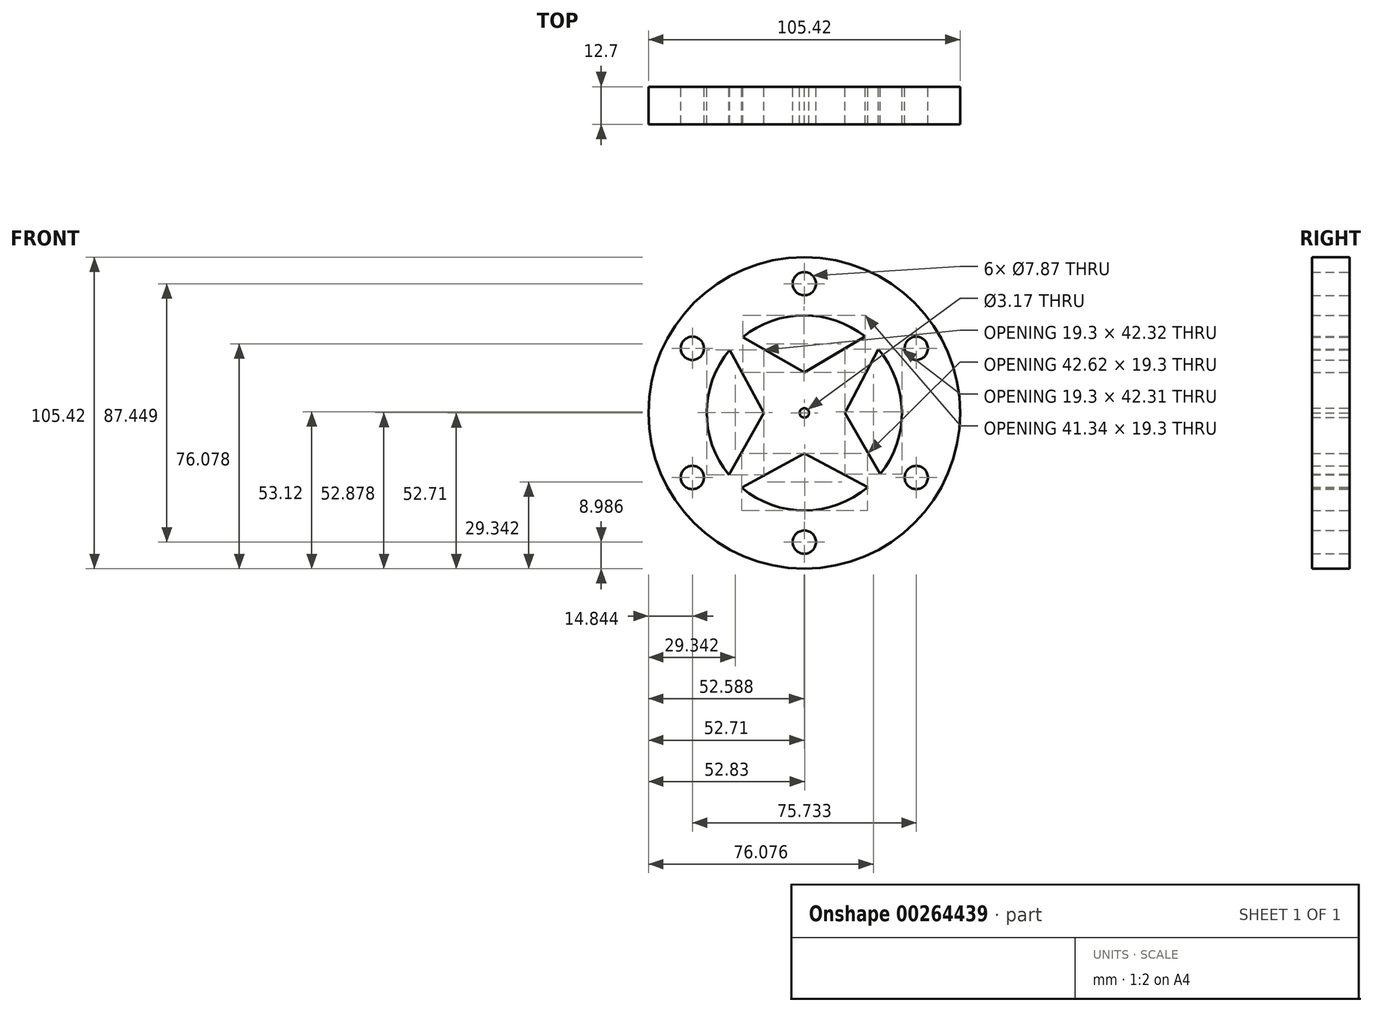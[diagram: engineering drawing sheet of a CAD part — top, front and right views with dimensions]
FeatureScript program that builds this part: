
annotation { "Feature Type Name" : "Feature", "Feature Type Description" : "" }
export const myFeature = defineFeature(function(context is Context, id is Id, definition is map)
    precondition{}
    {
        {
            var Q0;
            Q0=qCreatedBy(makeId("Front.planeOp"),FACE);
            var sketch = newSketch(context, id + "F0", { "sketchPlane" : qUnion([Q0])});
            skCircle(sketch, "E0", {"center": v(0, 0) * mm, "radius": 52.7 * mm});
            skCircle(sketch, "E1", {"center": v(0, 0) * mm, "radius": 1.59 * mm});
            skArc(sketch, "E2", {"start": v(-25.21, 21.33) * mm, "mid": v(-33.02, 0.22) * mm, "end": v(-25.49, -21) * mm});
            skLineSegment(sketch, "E3", {"start": v(-13.72, 0) * mm, "end": v(-25.21, 21.33) * mm});
            skLineSegment(sketch, "E4", {"start": v(-25.49, -21) * mm, "end": v(-13.72, 0) * mm});
            skLineSegment(sketch, "E5", {"start": v(0, -13.72) * mm, "end": v(-21.19, -25.32) * mm});
            skLineSegment(sketch, "E6", {"start": v(-20.8, 25.65) * mm, "end": v(0, 13.72) * mm});
            skLineSegment(sketch, "E7", {"start": v(20.55, 25.85) * mm, "end": v(0, 13.72) * mm});
            skLineSegment(sketch, "E8", {"start": v(25, 21.56) * mm, "end": v(13.72, 0) * mm});
            skLineSegment(sketch, "E9", {"start": v(21.43, -25.12) * mm, "end": v(0, -13.72) * mm});
            skLineSegment(sketch, "E10", {"start": v(25.69, -20.75) * mm, "end": v(13.72, 0) * mm});
            skArc(sketch, "E11.trimOffspring", {"start": v(-21.19, -25.32) * mm, "mid": v(0.16, -33.02) * mm, "end": v(21.43, -25.12) * mm});
            skArc(sketch, "E12.trimOffspring", {"start": v(25.69, -20.75) * mm, "mid": v(33.02, 0.53) * mm, "end": v(25, 21.56) * mm});
            skArc(sketch, "E13.trimOffspring", {"start": v(20.55, 25.85) * mm, "mid": v(-0.16, 33.02) * mm, "end": v(-20.8, 25.65) * mm});
            skLineSegment(sketch, "E14.anchor1", {"start": v(0, 0) * mm, "end": v(0, 43.72) * mm, "construction": true});
            skLineSegment(sketch, "E14.anchor2", {"start": v(0, 0) * mm, "end": v(0, 43.72) * mm, "construction": true});
            skCircle(sketch, "E15", {"center": v(0, 43.72) * mm, "radius": 3.94 * mm});
            skCircle(sketch, "E16.1.0", {"center": v(-37.87, 21.86) * mm, "radius": 3.94 * mm});
            skCircle(sketch, "E16.2.0", {"center": v(-37.87, -21.86) * mm, "radius": 3.94 * mm});
            skCircle(sketch, "E16.3.0", {"center": v(0, -43.72) * mm, "radius": 3.94 * mm});
            skCircle(sketch, "E16.4.0", {"center": v(37.87, -21.86) * mm, "radius": 3.94 * mm});
            skCircle(sketch, "E16.5.0", {"center": v(37.87, 21.86) * mm, "radius": 3.94 * mm});
            skSolve(sketch);
        }
        {
            var Q0;
            Q0=makeQuery(id+"F0.imprint","IMPRINT",FACE,{"disambiguationData":[TD([[makeQuery(id+"F0.imprint","IMPRINT",EDGE,{"derivedFrom":sQuery(id+"F0.wireOp",EDGE,"E0")}),1.0]])]});
            extrude(context, id + "F1", {"entities" : qUnion([Q0]), "depth" : 12.7 * mm});
        }
    });
